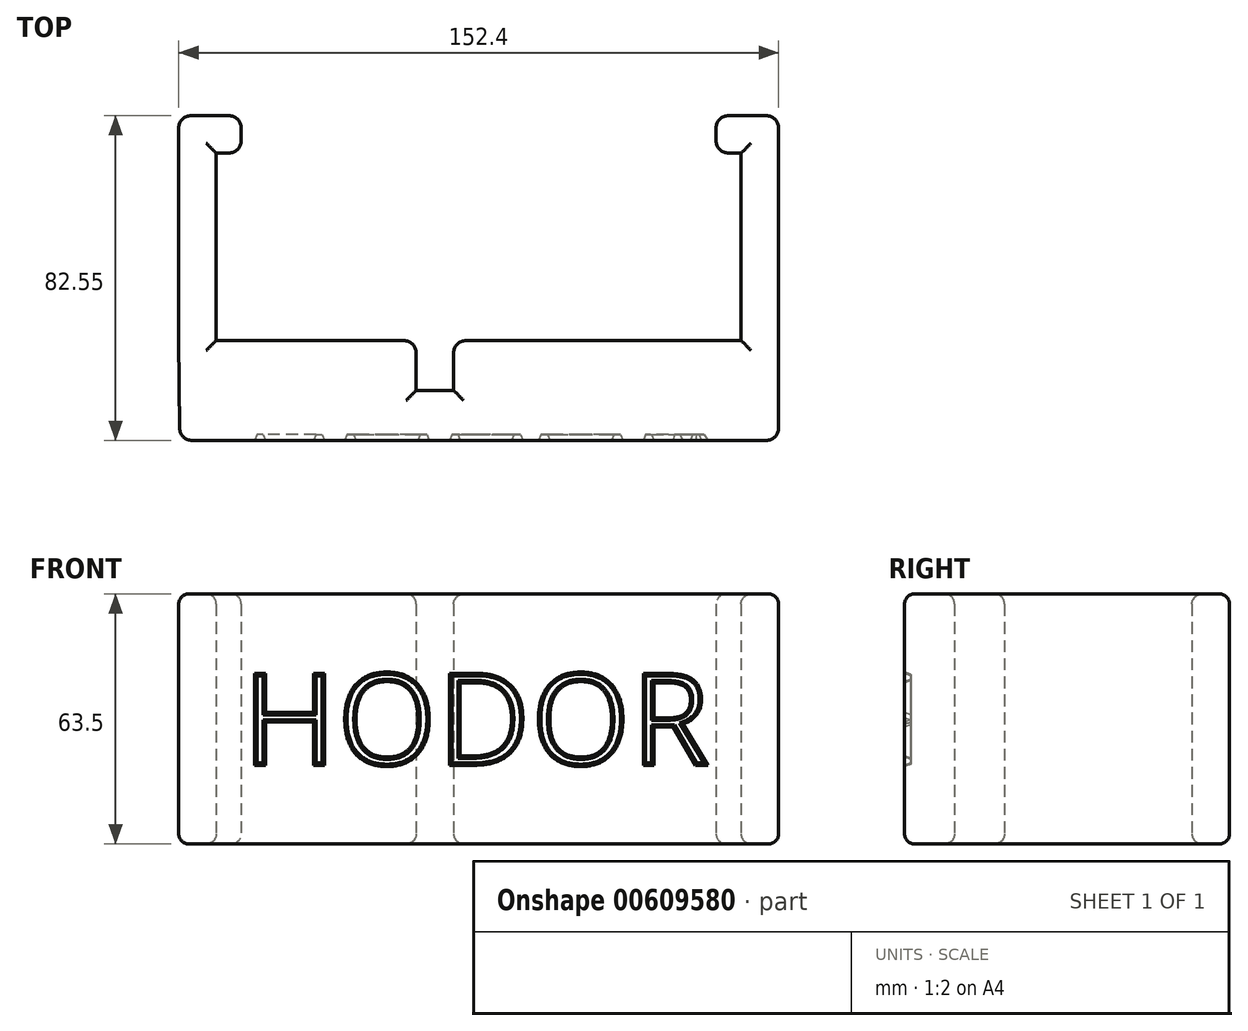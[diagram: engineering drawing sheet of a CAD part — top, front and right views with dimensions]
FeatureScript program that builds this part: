
annotation { "Feature Type Name" : "Feature", "Feature Type Description" : "" }
export const myFeature = defineFeature(function(context is Context, id is Id, definition is map)
    precondition{}
    {
        {
            var Q0;
            Q0=qCreatedBy(makeId("Top.planeOp"),FACE);
            var sketch = newSketch(context, id + "F0", { "sketchPlane" : qUnion([Q0])});
            skLineSegment(sketch, "E0", {"start": v(-60.33, 60.33) * mm, "end": v(-60.33, 12.7) * mm});
            skLineSegment(sketch, "E1", {"start": v(-60.33, 12.7) * mm, "end": v(-9.52, 12.7) * mm});
            skLineSegment(sketch, "E2", {"start": v(-9.53, 12.7) * mm, "end": v(-9.52, 0) * mm});
            skLineSegment(sketch, "E3", {"start": v(-9.52, 0) * mm, "end": v(0, 0) * mm});
            skLineSegment(sketch, "E4", {"start": v(0, 0) * mm, "end": v(0, 12.7) * mm});
            skLineSegment(sketch, "E5", {"start": v(0, 12.7) * mm, "end": v(73.03, 12.7) * mm});
            skLineSegment(sketch, "E6", {"start": v(73.03, 12.7) * mm, "end": v(73.03, 60.33) * mm});
            skLineSegment(sketch, "E7", {"start": v(73.03, 60.33) * mm, "end": v(66.68, 60.33) * mm});
            skLineSegment(sketch, "E8", {"start": v(66.67, 60.33) * mm, "end": v(66.67, 69.85) * mm});
            skLineSegment(sketch, "E9", {"start": v(66.68, 69.85) * mm, "end": v(82.55, 69.85) * mm});
            skLineSegment(sketch, "E10", {"start": v(82.55, 69.85) * mm, "end": v(82.55, -12.7) * mm});
            skLineSegment(sketch, "E11", {"start": v(-69.85, 12.7) * mm, "end": v(-69.85, 69.85) * mm});
            skLineSegment(sketch, "E12", {"start": v(-69.85, 69.85) * mm, "end": v(-53.98, 69.85) * mm});
            skLineSegment(sketch, "E13", {"start": v(-53.98, 69.85) * mm, "end": v(-53.98, 60.33) * mm});
            skLineSegment(sketch, "E14", {"start": v(-53.98, 60.33) * mm, "end": v(-60.33, 60.33) * mm});
            skLineSegment(sketch, "E15", {"start": v(-60.33, 12.7) * mm, "end": v(-60.33, -901.7) * mm, "construction": true});
            skLineSegment(sketch, "E16", {"start": v(-60.32, -901.7) * mm, "end": v(-69.85, 12.7) * mm, "construction": true});
            skLineSegment(sketch, "E17", {"start": v(-69.85, 12.7) * mm, "end": v(-69.59, -12.7) * mm});
            skLineSegment(sketch, "E18", {"start": v(-69.59, -12.7) * mm, "end": v(82.55, -12.7) * mm});
            skSolve(sketch);
        }
        {
            var Q0;
            Q0 = qSketchRegion(id + "F0", true);
            extrude(context, id + "F1", {"entities" : qUnion([Q0]), "depth" : 63.5 * mm, "offsetDistance" : 25.4 * mm});
        }
        {
            var Q0;
            Q0=makeQuery(id+"F1.opExtrude","SWEPT_EDGE",EDGE,{"disambiguationData":[OSD([sQuery(id+"F0.wireOp",EDGE,"E1"),sQuery(id+"F0.wireOp",EDGE,"E2")])]});
            var Q1;
            Q1=makeQuery(id+"F1.opExtrude","SWEPT_EDGE",EDGE,{"disambiguationData":[OSD([sQuery(id+"F0.wireOp",EDGE,"E4"),sQuery(id+"F0.wireOp",EDGE,"E5")])]});
            var Q2;
            Q2=makeQuery(id+"F1.opExtrude","SWEPT_EDGE",EDGE,{"disambiguationData":[OSD([sQuery(id+"F0.wireOp",EDGE,"E7"),sQuery(id+"F0.wireOp",EDGE,"E8")])]});
            var Q3;
            Q3=makeQuery(id+"F1.opExtrude","SWEPT_EDGE",EDGE,{"disambiguationData":[OSD([sQuery(id+"F0.wireOp",EDGE,"E13"),sQuery(id+"F0.wireOp",EDGE,"E14")])]});
            var Q4;
            Q4=makeQuery(id+"F1.opExtrude","SWEPT_EDGE",EDGE,{"disambiguationData":[OSD([sQuery(id+"F0.wireOp",EDGE,"E12"),sQuery(id+"F0.wireOp",EDGE,"E13")])]});
            var Q5;
            Q5=makeQuery(id+"F1.opExtrude","SWEPT_EDGE",EDGE,{"disambiguationData":[OSD([sQuery(id+"F0.wireOp",EDGE,"E11"),sQuery(id+"F0.wireOp",EDGE,"E12")])]});
            var Q6;
            Q6=makeQuery(id+"F1.opExtrude","SWEPT_EDGE",EDGE,{"disambiguationData":[OSD([sQuery(id+"F0.wireOp",EDGE,"E9"),sQuery(id+"F0.wireOp",EDGE,"E10")])]});
            var Q7;
            Q7=makeQuery(id+"F1.opExtrude","SWEPT_EDGE",EDGE,{"disambiguationData":[OSD([sQuery(id+"F0.wireOp",EDGE,"E8"),sQuery(id+"F0.wireOp",EDGE,"E9")])]});
            var Q8;
            Q8=makeQuery(id+"F1.opExtrude","SWEPT_EDGE",EDGE,{"disambiguationData":[OSD([sQuery(id+"F0.wireOp",EDGE,"E11"),sQuery(id+"F0.wireOp",EDGE,"E17")])]});
            var Q9;
            Q9=makeQuery(id+"F1.opExtrude","SWEPT_EDGE",EDGE,{"disambiguationData":[OSD([sQuery(id+"F0.wireOp",EDGE,"E17"),sQuery(id+"F0.wireOp",EDGE,"E18")])]});
            var Q10;
            Q10=makeQuery(id+"F1.opExtrude","SWEPT_EDGE",EDGE,{"disambiguationData":[OSD([sQuery(id+"F0.wireOp",EDGE,"E10"),sQuery(id+"F0.wireOp",EDGE,"E18")])]});
            fillet(context, id + "F2", {"entities" : qUnion([Q0, Q1, Q2, Q3, Q4, Q5, Q6, Q7, Q8, Q9, Q10]), "radius" : 3.17 * mm, "tangentPropagation" : true, "allowEdgeOverflow" : false});
        }
        {
            var Q0;
            Q0=makeQuery(id+"F1.opExtrude","CAP_FACE",FACE,{"disambiguationData":[OSD([sQuery(id+"F0.wireOp",EDGE,"E0"),sQuery(id+"F0.wireOp",EDGE,"E1"),sQuery(id+"F0.wireOp",EDGE,"E2"),sQuery(id+"F0.wireOp",EDGE,"E3"),sQuery(id+"F0.wireOp",EDGE,"E4"),sQuery(id+"F0.wireOp",EDGE,"E5"),sQuery(id+"F0.wireOp",EDGE,"E6"),sQuery(id+"F0.wireOp",EDGE,"E7"),sQuery(id+"F0.wireOp",EDGE,"E8"),sQuery(id+"F0.wireOp",EDGE,"E9"),sQuery(id+"F0.wireOp",EDGE,"E10"),sQuery(id+"F0.wireOp",EDGE,"E11"),sQuery(id+"F0.wireOp",EDGE,"E12"),sQuery(id+"F0.wireOp",EDGE,"E13"),sQuery(id+"F0.wireOp",EDGE,"E14"),sQuery(id+"F0.wireOp",EDGE,"E17"),sQuery(id+"F0.wireOp",EDGE,"E18")])],"isStart":false});
            var Q1;
            Q1=makeQuery(id+"F1.opExtrude","CAP_FACE",FACE,{"disambiguationData":[OSD([sQuery(id+"F0.wireOp",EDGE,"E0"),sQuery(id+"F0.wireOp",EDGE,"E1"),sQuery(id+"F0.wireOp",EDGE,"E2"),sQuery(id+"F0.wireOp",EDGE,"E3"),sQuery(id+"F0.wireOp",EDGE,"E4"),sQuery(id+"F0.wireOp",EDGE,"E5"),sQuery(id+"F0.wireOp",EDGE,"E6"),sQuery(id+"F0.wireOp",EDGE,"E7"),sQuery(id+"F0.wireOp",EDGE,"E8"),sQuery(id+"F0.wireOp",EDGE,"E9"),sQuery(id+"F0.wireOp",EDGE,"E10"),sQuery(id+"F0.wireOp",EDGE,"E11"),sQuery(id+"F0.wireOp",EDGE,"E12"),sQuery(id+"F0.wireOp",EDGE,"E13"),sQuery(id+"F0.wireOp",EDGE,"E14"),sQuery(id+"F0.wireOp",EDGE,"E17"),sQuery(id+"F0.wireOp",EDGE,"E18")])],"isStart":true});
            fillet(context, id + "F3", {"entities" : qUnion([Q0, Q1]), "radius" : 2.54 * mm, "tangentPropagation" : true, "allowEdgeOverflow" : false});
        }
        {
            var Q0;
            Q0=makeQuery(id+"F1.opExtrude","SWEPT_FACE",FACE,{"disambiguationData":[OSD([sQuery(id+"F0.wireOp",EDGE,"E18")])]});
            var sketch = newSketch(context, id + "F4", { "sketchPlane" : qUnion([Q0])});
            skText(sketch, "E19", { "text": "HODOR", "fontName": "OpenSans-Regular.ttf"});
            skPoint(sketch, "E20", {"position": v(6.47, 31.75) * mm});
            skPoint(sketch, "E21", {"position": v(79.38, 31.75) * mm});
            const initialGuessF4  = {"E19": [-0.05374, 0.02, 1, 0, 0.0235]};
            skSetInitialGuess(sketch, initialGuessF4);
            skSolve(sketch);
        }
        {
            var Q0;
            Q0 = qSketchRegion(id + "F4", true);
            extrude(context, id + "F5", {"entities" : qUnion([Q0]), "operationType" : NewBodyOperationType.REMOVE, "oppositeDirection" : true, "depth" : 1.59 * mm, "offsetDistance" : 25.4 * mm, "hasDraft" : true, "draftAngle" : 20 * degree, "draftPullDirection" : true});
        }
    });
